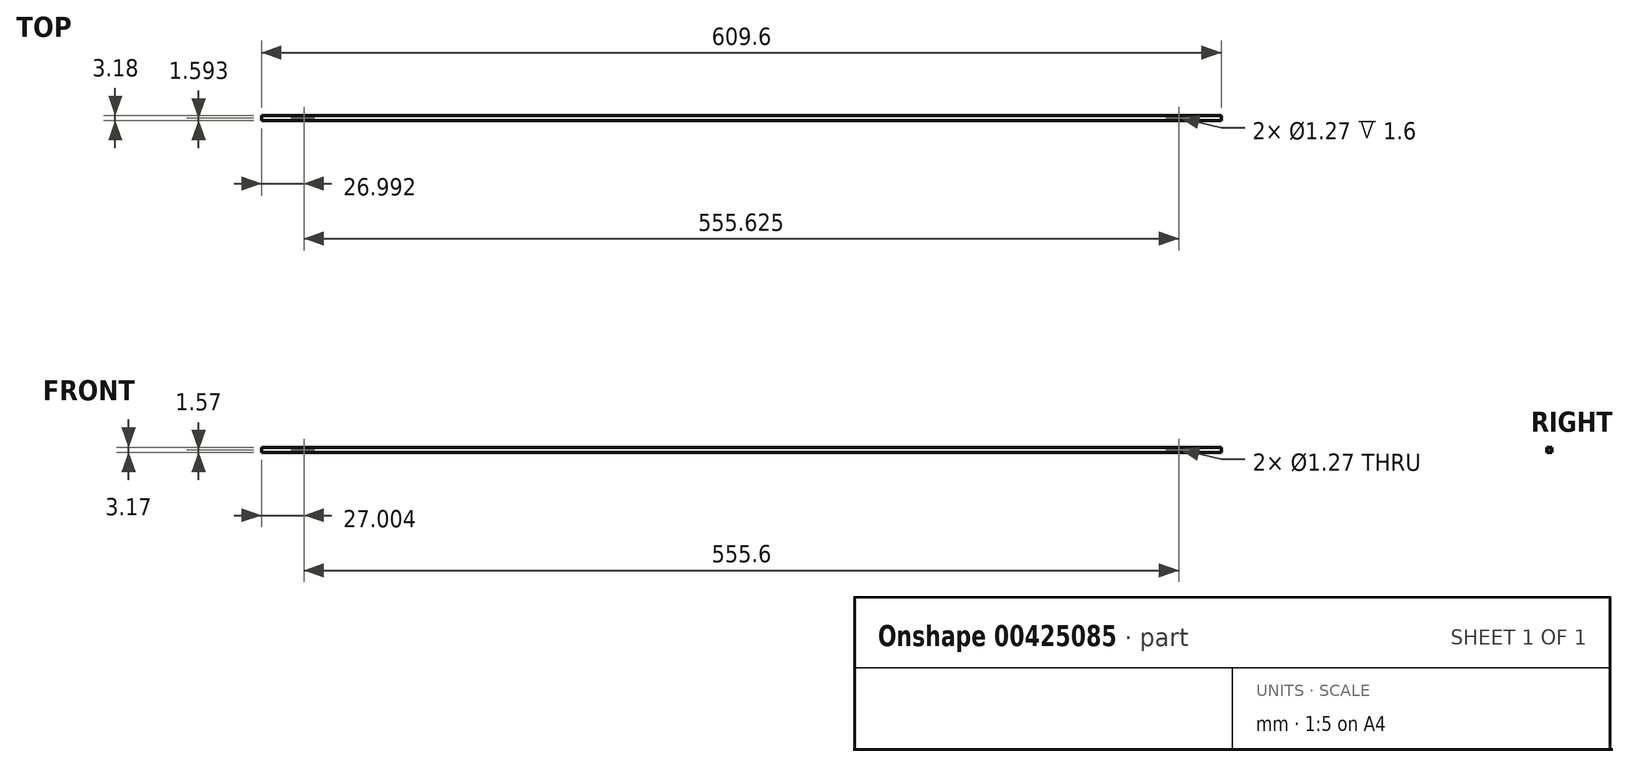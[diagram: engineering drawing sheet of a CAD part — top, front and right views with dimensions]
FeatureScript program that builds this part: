
annotation { "Feature Type Name" : "Feature", "Feature Type Description" : "" }
export const myFeature = defineFeature(function(context is Context, id is Id, definition is map)
    precondition{}
    {
        {
            var Q0;
            Q0=qCreatedBy(makeId("Front.planeOp"),FACE);
            var sketch = newSketch(context, id + "F0", { "sketchPlane" : qUnion([Q0])});
            skLineSegment(sketch, "E0", {"start": v(-319.33, -3.17) * mm, "end": v(290.27, -3.17) * mm});
            skLineSegment(sketch, "E1", {"start": v(-319.33, -3.17) * mm, "end": v(-293.93, -3.17) * mm});
            skLineSegment(sketch, "E2", {"start": v(290.27, -3.17) * mm, "end": v(264.87, -3.17) * mm});
            skLineSegment(sketch, "E3", {"start": v(-319.33, -3.17) * mm, "end": v(-319.33, 0) * mm});
            skLineSegment(sketch, "E4", {"start": v(-319.33, 0) * mm, "end": v(290.27, 0) * mm});
            skLineSegment(sketch, "E5", {"start": v(290.27, 0) * mm, "end": v(290.27, -3.17) * mm});
            skSolve(sketch);
        }
        {
            var Q0;
            Q0 = qSketchRegion(id + "F0", true);
            extrude(context, id + "F1", {"entities" : qUnion([Q0]), "depth" : 3.17 * mm});
        }
        {
            var Q0;
            Q0=qCreatedBy(makeId("Top.planeOp"),FACE);
            var sketch = newSketch(context, id + "F2", { "sketchPlane" : qUnion([Q0])});
            skCircle(sketch, "E6", {"center": v(-292.34, -1.59) * mm, "radius": 0.64 * mm});
            skCircle(sketch, "E7", {"center": v(263.29, -1.59) * mm, "radius": 0.64 * mm});
            skSolve(sketch);
        }
        {
            var Q0;
            Q0 = qSketchRegion(id + "F2", true);
            extrude(context, id + "F3", {"entities" : qUnion([Q0]), "operationType" : NewBodyOperationType.REMOVE, "oppositeDirection" : true, "depth" : 1.6 * mm});
        }
        {
            var Q0;
            Q0=makeQuery(id+"F1.opExtrude","CAP_FACE",FACE,{"disambiguationData":[OSD([sQuery(id+"F0.wireOp",EDGE,"E0"),sQuery(id+"F0.wireOp",EDGE,"E1"),sQuery(id+"F0.wireOp",EDGE,"E2"),sQuery(id+"F0.wireOp",EDGE,"E3"),sQuery(id+"F0.wireOp",EDGE,"E4"),sQuery(id+"F0.wireOp",EDGE,"E5")])],"isStart":false});
            var sketch = newSketch(context, id + "F4", { "sketchPlane" : qUnion([Q0])});
            skCircle(sketch, "E8", {"center": v(-292.33, -1.6) * mm, "radius": 0.64 * mm});
            skCircle(sketch, "E9", {"center": v(263.27, -1.6) * mm, "radius": 0.64 * mm});
            skSolve(sketch);
        }
        {
            var Q0;
            Q0 = qSketchRegion(id + "F4", true);
            extrude(context, id + "F5", {"entities" : qUnion([Q0]), "operationType" : NewBodyOperationType.REMOVE, "oppositeDirection" : true, "depth" : 25.4 * mm});
        }
    });
